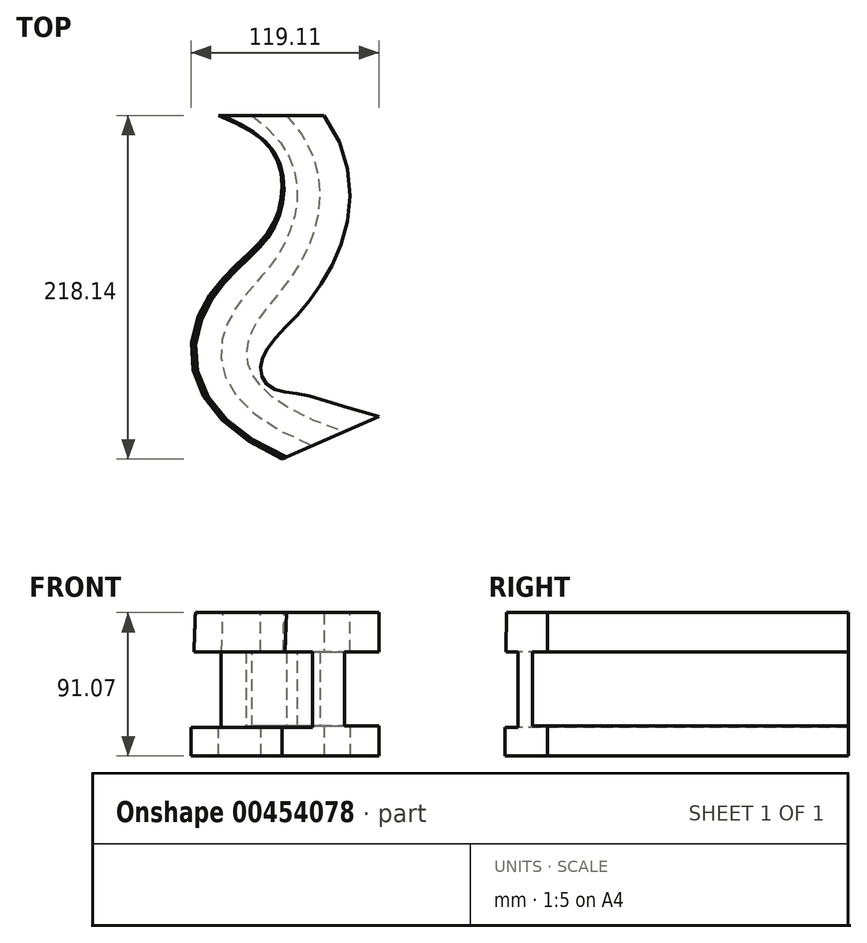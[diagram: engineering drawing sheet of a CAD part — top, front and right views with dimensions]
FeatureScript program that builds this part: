
annotation { "Feature Type Name" : "Feature", "Feature Type Description" : "" }
export const myFeature = defineFeature(function(context is Context, id is Id, definition is map)
    precondition{}
    {
        {
            var Q0;
            Q0=qCreatedBy(makeId("Front.planeOp"),FACE);
            var sketch = newSketch(context, id + "F0", { "sketchPlane" : qUnion([Q0])});
            skLineSegment(sketch, "E0", {"start": v(-33.55, 50.09) * mm, "end": v(30.68, 50.09) * mm});
            skLineSegment(sketch, "E1", {"start": v(30.68, 50.09) * mm, "end": v(30.68, 25.16) * mm});
            skLineSegment(sketch, "E2", {"start": v(30.68, 25.16) * mm, "end": v(6.71, 25.16) * mm});
            skLineSegment(sketch, "E3", {"start": v(6.71, 25.16) * mm, "end": v(6.71, -21.8) * mm});
            skLineSegment(sketch, "E4", {"start": v(6.71, -21.8) * mm, "end": v(30.68, -21.8) * mm});
            skLineSegment(sketch, "E5", {"start": v(30.68, -21.8) * mm, "end": v(30.68, -40.98) * mm});
            skLineSegment(sketch, "E6", {"start": v(30.68, -40.98) * mm, "end": v(-36.43, -40.98) * mm});
            skLineSegment(sketch, "E7", {"start": v(-36.43, -40.98) * mm, "end": v(-36.43, -22.77) * mm});
            skLineSegment(sketch, "E8", {"start": v(-36.43, -22.77) * mm, "end": v(-15.34, -22.77) * mm});
            skLineSegment(sketch, "E9", {"start": v(-15.34, -22.77) * mm, "end": v(-15.34, 25.16) * mm});
            skLineSegment(sketch, "E10", {"start": v(-15.34, 25.16) * mm, "end": v(-34.51, 25.16) * mm});
            skLineSegment(sketch, "E11", {"start": v(-34.51, 25.16) * mm, "end": v(-33.55, 50.09) * mm});
            skSolve(sketch);
        }
        {
            var Q0;
            Q0=qCreatedBy(makeId("Top.planeOp"),FACE);
            var sketch = newSketch(context, id + "F1", { "sketchPlane" : qUnion([Q0])});
            skFitSpline(sketch, "E12", {"points": [v(0, 0) * mm, v(11.42, -91.03) * mm, v(-19.66, -135.79) * mm, v(37.25, -203.4) * mm], "startDerivative": vector(270.83, -253.69) * mm, "endDerivative": vector(520.63, -181.78) * mm});
            skSolve(sketch);
        }
        {
            var Q0;
            Q0=makeQuery(id+"F0.imprint","IMPRINT",FACE,{"disambiguationData":[TD([[makeQuery(id+"F0.imprint","IMPRINT",EDGE,{"derivedFrom":sQuery(id+"F0.wireOp",EDGE,"E0")}),-1.0]])]});
            var Q1;
            Q1=sQuery(id+"F1.wireOp",EDGE,"E12");
            sweep(context, id + "F2", {"profiles" : qUnion([Q0]), "path" : qUnion([Q1])});
        }
    });
